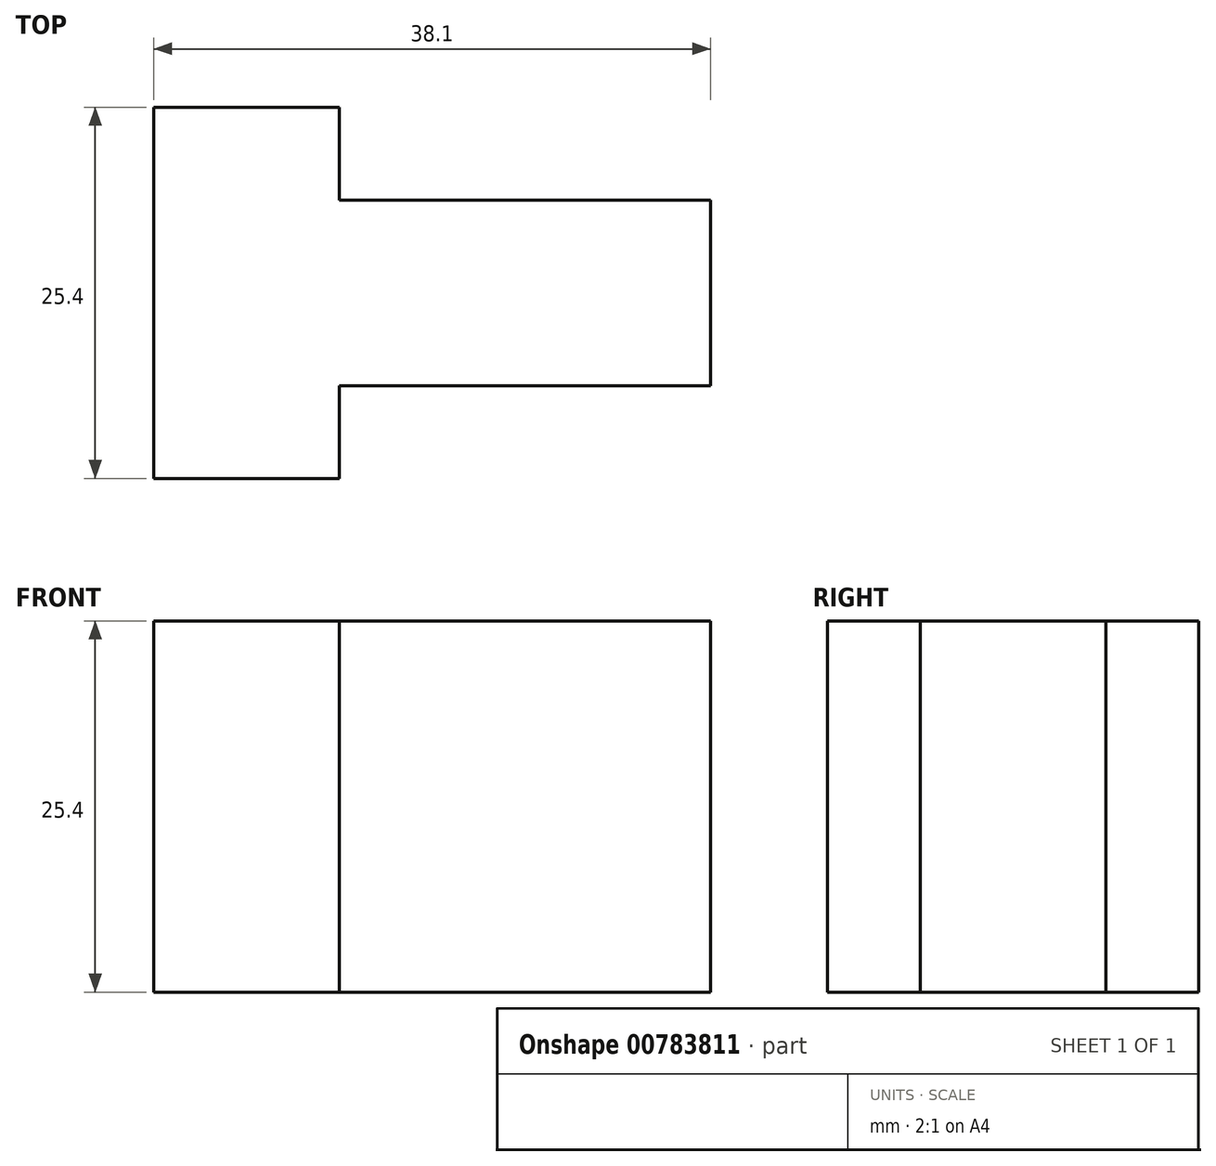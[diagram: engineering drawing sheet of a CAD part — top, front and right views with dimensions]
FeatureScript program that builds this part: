
annotation { "Feature Type Name" : "Feature", "Feature Type Description" : "" }
export const myFeature = defineFeature(function(context is Context, id is Id, definition is map)
    precondition{}
    {
        {
            var Q0;
            Q0=qCreatedBy(makeId("Top.planeOp"),FACE);
            var sketch = newSketch(context, id + "F0", { "sketchPlane" : qUnion([Q0])});
            skLineSegment(sketch, "E0", {"start": v(0, 0) * mm, "end": v(12.7, 0) * mm});
            skLineSegment(sketch, "E1", {"start": v(0, 0) * mm, "end": v(0, 25.4) * mm});
            skLineSegment(sketch, "E2", {"start": v(0, 25.4) * mm, "end": v(12.7, 25.4) * mm});
            skLineSegment(sketch, "E3", {"start": v(12.7, 0) * mm, "end": v(12.7, 6.35) * mm});
            skLineSegment(sketch, "E4", {"start": v(12.7, 25.4) * mm, "end": v(12.7, 19.05) * mm});
            skLineSegment(sketch, "E5", {"start": v(12.7, 6.35) * mm, "end": v(38.1, 6.35) * mm});
            skLineSegment(sketch, "E6", {"start": v(12.7, 19.05) * mm, "end": v(38.1, 19.05) * mm});
            skLineSegment(sketch, "E7", {"start": v(38.1, 6.35) * mm, "end": v(38.1, 19.05) * mm});
            skSolve(sketch);
        }
        {
            var Q0;
            Q0=makeQuery(id+"F0.imprint","IMPRINT",FACE,{"disambiguationData":[TD([[makeQuery(id+"F0.imprint","IMPRINT",EDGE,{"derivedFrom":sQuery(id+"F0.wireOp",EDGE,"E0")}),1.0]])]});
            extrude(context, id + "F1", {"entities" : qUnion([Q0]), "depth" : 25.4 * mm, "offsetDistance" : 25.4 * mm});
        }
    });
